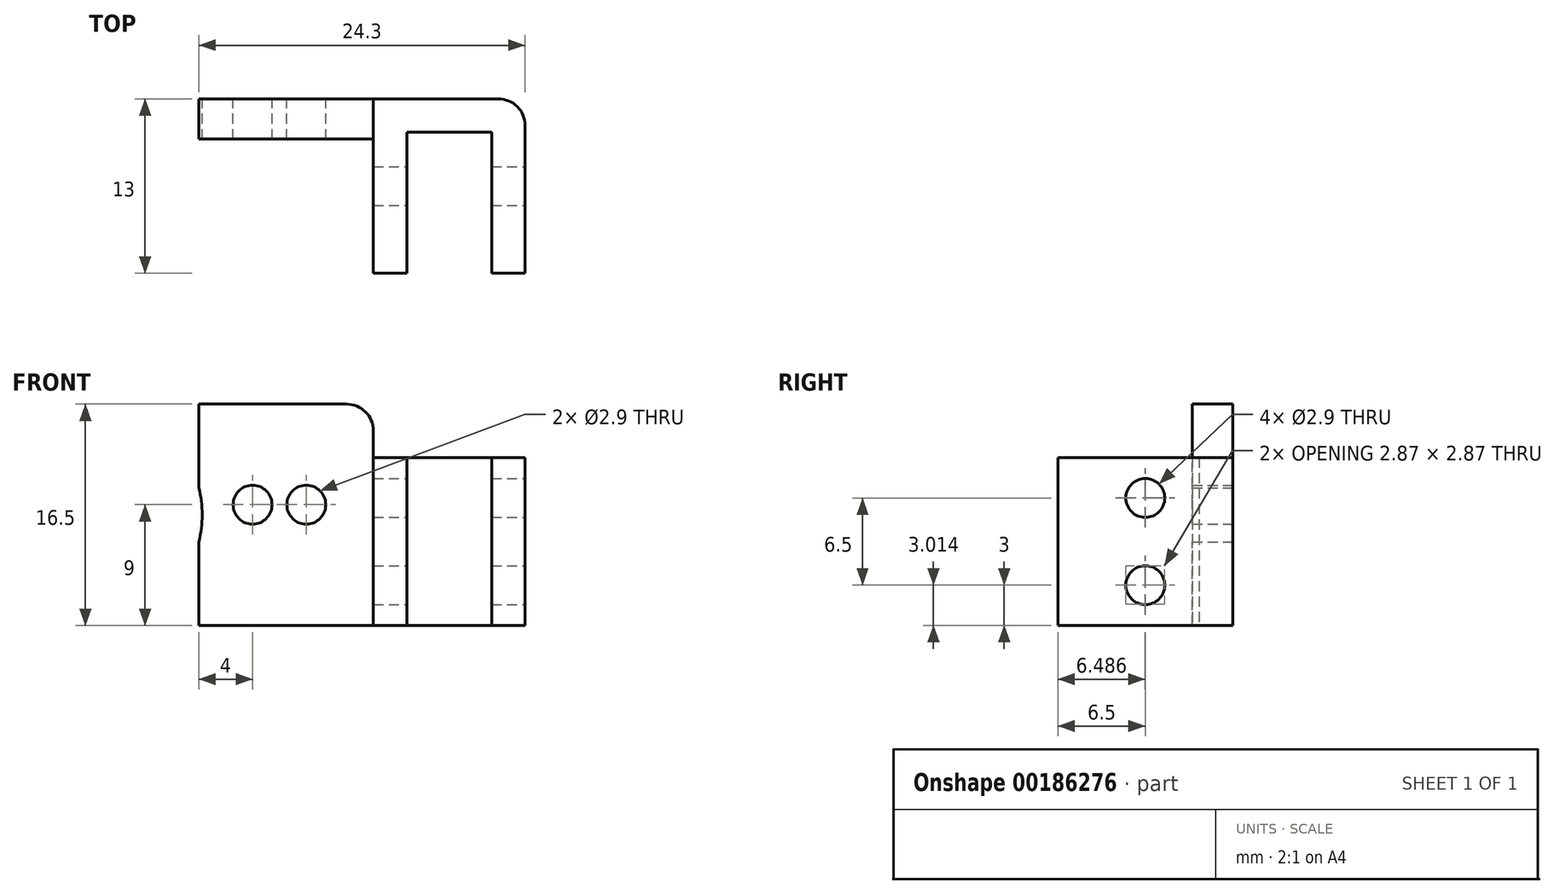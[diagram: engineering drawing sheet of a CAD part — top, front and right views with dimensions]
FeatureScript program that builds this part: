
annotation { "Feature Type Name" : "Feature", "Feature Type Description" : "" }
export const myFeature = defineFeature(function(context is Context, id is Id, definition is map)
    precondition{}
    {
        {
            var Q0;
            Q0=qCreatedBy(makeId("Top.planeOp"),FACE);
            var sketch = newSketch(context, id + "F0", { "sketchPlane" : qUnion([Q0])});
            skLineSegment(sketch, "E0.bottom", {"start": v(3.15, -4) * mm, "end": v(-3.15, -4) * mm});
            skLineSegment(sketch, "E0.top", {"start": v(3.15, 4) * mm, "end": v(-3.15, 4) * mm});
            skLineSegment(sketch, "E0.left", {"start": v(3.15, -4) * mm, "end": v(3.15, 4) * mm});
            skLineSegment(sketch, "E0.right", {"start": v(-3.15, -4) * mm, "end": v(-3.15, 4) * mm});
            skPoint(sketch, "E0.middle", {"position": v(0, 0) * mm});
            skLineSegment(sketch, "E1.0", {"start": v(5.65, 6.5) * mm, "end": v(-5.65, 6.5) * mm});
            skLineSegment(sketch, "E1.1", {"start": v(5.65, -6.5) * mm, "end": v(5.65, 6.5) * mm});
            skLineSegment(sketch, "E1.2", {"start": v(5.65, -6.5) * mm, "end": v(-5.65, -6.5) * mm});
            skLineSegment(sketch, "E1.3", {"start": v(-5.65, -6.5) * mm, "end": v(-5.65, 6.5) * mm});
            skLineSegment(sketch, "E2", {"start": v(3.15, -4) * mm, "end": v(3.15, -6.5) * mm});
            skPoint(sketch, "E2.endSnap0", {"position": v(0, -6.5) * mm});
            skLineSegment(sketch, "E3", {"start": v(3.15, -6.5) * mm, "end": v(-3.15, -6.5) * mm});
            skLineSegment(sketch, "E4", {"start": v(-3.15, -6.5) * mm, "end": v(-3.15, -4) * mm});
            skPoint(sketch, "E5", {"position": v(-5.65, 6.5) * mm});
            skPoint(sketch, "E6", {"position": v(-30.65, 6.5) * mm});
            skPoint(sketch, "E7", {"position": v(-30.65, 3.5) * mm});
            skPoint(sketch, "E8", {"position": v(-5.65, 3.5) * mm});
            skLineSegment(sketch, "E9", {"start": v(-5.65, 6.5) * mm, "end": v(-30.65, 6.5) * mm});
            skLineSegment(sketch, "E10", {"start": v(-30.65, 6.5) * mm, "end": v(-30.65, 3.5) * mm});
            skLineSegment(sketch, "E11", {"start": v(-30.65, 3.5) * mm, "end": v(-5.65, 3.5) * mm});
            skSolve(sketch);
        }
        {
            var Q0;
            {var subQ0=sQuery(id+"F0.wireOp",EDGE,"E9");Q0=makeQuery(id+"F0.imprint","IMPRINT",FACE,{"disambiguationData":[TD([[makeQuery(id+"F0.imprint","IMPRINT",EDGE,{"derivedFrom":subQ0}),1.0]])]});}
            var Q1;
            Q1=makeQuery(id+"F0.imprint","IMPRINT",FACE,{"disambiguationData":[TD([[makeQuery(id+"F0.imprint","IMPRINT",EDGE,{"derivedFrom":sQuery(id+"F0.wireOp",EDGE,"E0.top")}),-1.0]])]});
            extrude(context, id + "F1", {"entities" : qUnion([Q0, Q1]), "depth" : 12.5 * mm, "offsetDistance" : 25 * mm});
        }
        {
            var Q0;
            Q0=makeQuery(id+"F1.opExtrude","CAP_FACE",FACE,{"disambiguationData":[OSD([sQuery(id+"F0.wireOp",EDGE,"E0.top"),sQuery(id+"F0.wireOp",EDGE,"E0.left"),sQuery(id+"F0.wireOp",EDGE,"E0.right"),sQuery(id+"F0.wireOp",EDGE,"E1.0"),sQuery(id+"F0.wireOp",EDGE,"E1.1"),sQuery(id+"F0.wireOp",EDGE,"E1.2"),sQuery(id+"F0.wireOp",EDGE,"E1.3"),sQuery(id+"F0.wireOp",EDGE,"E2"),sQuery(id+"F0.wireOp",EDGE,"E4"),sQuery(id+"F0.wireOp",EDGE,"E9"),sQuery(id+"F0.wireOp",EDGE,"E10"),sQuery(id+"F0.wireOp",EDGE,"E11")])],"isStart":false});
            var sketch = newSketch(context, id + "F2", { "sketchPlane" : qUnion([Q0])});
            skPoint(sketch, "E12", {"position": v(-5.65, 3.5) * mm});
            skPoint(sketch, "E13", {"position": v(-5.65, 6.5) * mm});
            skPoint(sketch, "E14", {"position": v(-30.65, 6.5) * mm});
            skPoint(sketch, "E15", {"position": v(-30.65, 3.5) * mm});
            skLineSegment(sketch, "E16", {"start": v(-5.65, 3.5) * mm, "end": v(-5.65, 6.5) * mm});
            skSolve(sketch);
        }
        {
            var Q0;
            {var subQ0=sQuery(id+"F2.wireOp",EDGE,"E16");Q0=makeQuery(id+"F2.imprint","IMPRINT",FACE,{"disambiguationData":[TD([[makeQuery(id+"F2.imprint","IMPRINT",EDGE,{"derivedFrom":subQ0}),1.0]])]});}
            extrude(context, id + "F3", {"entities" : qUnion([Q0]), "operationType" : NewBodyOperationType.ADD, "depth" : 4 * mm, "offsetDistance" : 25 * mm});
        }
        {
            var Q0;
            Q0=makeQuery(id+"F1.opExtrude","SWEPT_FACE",FACE,{"disambiguationData":[OSD([sQuery(id+"F0.wireOp",EDGE,"E1.0"),sQuery(id+"F0.wireOp",EDGE,"E9")])]});
            var sketch = newSketch(context, id + "F4", { "sketchPlane" : qUnion([Q0])});
            skPoint(sketch, "E17", {"position": v(30.65, 8.25) * mm});
            skPoint(sketch, "E18", {"position": v(26.65, 8.25) * mm});
            skCircle(sketch, "E19", {"center": v(26.65, 8.25) * mm, "radius": 4.5 * mm});
            skCircle(sketch, "E20", {"center": v(26.65, 8.25) * mm, "radius": 8.25 * mm});
            skSolve(sketch);
        }
        {
            var Q0;
            {var subQ0=sQuery(id+"F4.wireOp",EDGE,"E20");var subQ1=sQuery(id+"F0.wireOp",EDGE,"E9");var subQ2=sQuery(id+"F0.wireOp",EDGE,"E1.0");var subQ3=makeQuery(id+"F3.opExtrude","CAP_EDGE",EDGE,{"disambiguationData":[OSD([subQ2,subQ1])],"isStart":false});var subQ4=makeQuery(id+"F4.imprint","INTERSECT",VERTEX,{"derivedFrom":[subQ3,subQ0]});Q0=makeQuery(id+"F4.imprint","IMPRINT",FACE,{"disambiguationData":[TD([[makeQuery(id+"F4.imprint","IMPRINT",EDGE,{"disambiguationData":[TD([[subQ4,1.0]])],"derivedFrom":subQ0}),-1.0]])]});}
            var Q1;
            {var subQ0=sQuery(id+"F4.wireOp",EDGE,"E20");var subQ1=sQuery(id+"F0.wireOp",EDGE,"E9");var subQ2=sQuery(id+"F0.wireOp",EDGE,"E1.0");var subQ3=makeQuery(id+"F1.opExtrude","CAP_EDGE",EDGE,{"disambiguationData":[OSD([subQ2,subQ1])],"isStart":true});var subQ4=makeQuery(id+"F4.imprint","INTERSECT",VERTEX,{"derivedFrom":[subQ3,subQ0]});Q1=makeQuery(id+"F4.imprint","IMPRINT",FACE,{"disambiguationData":[TD([[makeQuery(id+"F4.imprint","IMPRINT",EDGE,{"disambiguationData":[TD([[subQ4,-1.0]])],"derivedFrom":subQ0}),-1.0]])]});}
            var Q2;
            {var subQ0=sQuery(id+"F4.wireOp",EDGE,"E19");var subQ1=sQuery(id+"F0.wireOp",EDGE,"E10");var subQ2=sQuery(id+"F0.wireOp",EDGE,"E9");var subQ3=makeQuery(id+"F3.boolean.opBoolean","MERGE",EDGE,{"derivedFrom":[makeQuery(id+"F1.opExtrude","SWEPT_EDGE",EDGE,{"disambiguationData":[OSD([subQ2,subQ1])]}),makeQuery(id+"F3.opExtrude","SWEPT_EDGE",EDGE,{"disambiguationData":[OSD([sQuery(id+"F0.wireOp",EDGE,"E1.0"),subQ2,subQ1])]})]});var subQ4=makeQuery(id+"F4.imprint","INTERSECT",VERTEX,{"disambiguationData":[OD(0.0)],"derivedFrom":[subQ3,subQ0]});Q2=makeQuery(id+"F4.imprint","IMPRINT",FACE,{"disambiguationData":[TD([[makeQuery(id+"F4.imprint","IMPRINT",EDGE,{"disambiguationData":[TD([[subQ4,-1.0]])],"derivedFrom":subQ0}),1.0]])]});}
            extrude(context, id + "F5", {"entities" : qUnion([Q0, Q1, Q2]), "operationType" : NewBodyOperationType.REMOVE, "oppositeDirection" : true, "depth" : 25 * mm, "offsetDistance" : 25 * mm});
        }
        {
            var Q0;
            {var subQ0=sQuery(id+"F4.wireOp",EDGE,"E20");var subQ1=sQuery(id+"F0.wireOp",EDGE,"E9");var subQ2=sQuery(id+"F0.wireOp",EDGE,"E1.0");var subQ10=makeQuery(id+"F4.imprint","INTERSECT",VERTEX,{"derivedFrom":[makeQuery(id+"F3.opExtrude","CAP_EDGE",EDGE,{"disambiguationData":[OSD([subQ2,subQ1])],"isStart":false}),subQ0]});Q0=makeQuery(id+"F4.imprint","IMPRINT",FACE,{"disambiguationData":[TD([[makeQuery(id+"F4.imprint","IMPRINT",EDGE,{"disambiguationData":[TD([[subQ10,-1.0]])],"derivedFrom":subQ0}),1.0]])]});}
            extrude(context, id + "F6", {"entities" : qUnion([Q0]), "operationType" : NewBodyOperationType.ADD, "depth" : 15 * mm, "offsetDistance" : 25 * mm});
        }
        {
            var Q0;
            Q0=makeQuery(id+"F1.opExtrude","SWEPT_FACE",FACE,{"disambiguationData":[OSD([sQuery(id+"F0.wireOp",EDGE,"E1.1")])]});
            var sketch = newSketch(context, id + "F7", { "sketchPlane" : qUnion([Q0])});
            skPoint(sketch, "E21", {"position": v(4, 0) * mm});
            skPoint(sketch, "E22", {"position": v(4, 3) * mm});
            skPoint(sketch, "E23", {"position": v(0, 3) * mm});
            skPoint(sketch, "E24", {"position": v(0, 9.5) * mm});
            skSolve(sketch);
        }
        {
            var Q0;
            Q0=sQuery(id+"F7.wireOp",VERTEX,"E23");
            var Q1;
            Q1=sQuery(id+"F7.wireOp",VERTEX,"E24");
            var Q2;
            Q2=makeQuery(id+"F1.opExtrude","SWEPT_BODY",BODY,{"disambiguationData":[OSD([sQuery(id+"F0.wireOp",EDGE,"E0.top"),sQuery(id+"F0.wireOp",EDGE,"E0.left"),sQuery(id+"F0.wireOp",EDGE,"E0.right"),sQuery(id+"F0.wireOp",EDGE,"E1.0"),sQuery(id+"F0.wireOp",EDGE,"E1.1"),sQuery(id+"F0.wireOp",EDGE,"E1.2"),sQuery(id+"F0.wireOp",EDGE,"E1.3"),sQuery(id+"F0.wireOp",EDGE,"E2"),sQuery(id+"F0.wireOp",EDGE,"E4"),sQuery(id+"F0.wireOp",EDGE,"E9"),sQuery(id+"F0.wireOp",EDGE,"E10"),sQuery(id+"F0.wireOp",EDGE,"E11")])]});
            hole(context, id + "F8", {"style" : HoleStyle.SIMPLE, "endStyle" : HoleEndStyle.THROUGH, "standardTappedOrClearance" : lookupTablePath({ "fit" : "Normal", "standard" : "ISO", "size" : "M2.5", "type" : "Clearance" }), "standardBlindInLast" : lookupTablePath({ "fit" : "Normal", "standard" : "ISO", "engagement" : "75%", "pitch" : "0.35 mm", "size" : "M2.5", "type" : "Clearance & tapped" }), "holeDiameter" : 2.9 * mm, "majorDiameter" : 5 * mm, "isTappedThrough" : true, "tappedDepth" : 12 * mm, "tapClearance" : 3, "startFromSketch" : true, "locations" : qUnion([Q0, Q1]), "scope" : qUnion([Q2])});
        }
        {
            var Q0;
            Q0=makeQuery(id+"F6.opExtrude","CAP_FACE",FACE,{"disambiguationData":[OSD([sQuery(id+"F0.wireOp",EDGE,"E1.0"),sQuery(id+"F0.wireOp",EDGE,"E9"),sQuery(id+"F0.wireOp",EDGE,"E10"),sQuery(id+"F4.wireOp",EDGE,"E19"),sQuery(id+"F4.wireOp",EDGE,"E20")])],"isStart":false});
            extrude(context, id + "F9", {"entities" : qUnion([Q0]), "operationType" : NewBodyOperationType.REMOVE, "oppositeDirection" : true, "depth" : 25 * mm, "offsetDistance" : 25 * mm});
        }
        {
            var Q0;
            {var subQ1=sQuery(id+"F0.wireOp",EDGE,"E1.0");var subQ3=makeQuery(id+"F1.opExtrude","SWEPT_EDGE",EDGE,{"disambiguationData":[OSD([subQ1,sQuery(id+"F0.wireOp",EDGE,"E1.1")])]});Q0=makeQuery(id+"F4.imprint","IMPRINT",FACE,{"disambiguationData":[TD([[makeQuery(id+"F4.imprint","IMPRINT",EDGE,{"derivedFrom":subQ3}),1.0]])]});}
            var sketch = newSketch(context, id + "F10", { "sketchPlane" : qUnion([Q0])});
            skPoint(sketch, "E25", {"position": v(18.65, 9) * mm});
            skPoint(sketch, "E26", {"position": v(18.65, 16.5) * mm});
            skPoint(sketch, "E27", {"position": v(18.65, 0) * mm});
            skLineSegment(sketch, "E28", {"start": v(18.65, 0) * mm, "end": v(18.65, 16.5) * mm});
            skPoint(sketch, "E29", {"position": v(14.65, 9) * mm});
            skPoint(sketch, "E30", {"position": v(10.65, 9) * mm});
            skPoint(sketch, "E31", {"position": v(6.65, 9) * mm});
            skSolve(sketch);
        }
        {
            var Q0;
            {var subQ0=sQuery(id+"F10.wireOp",EDGE,"E28");var subQ1=sQuery(id+"F0.wireOp",EDGE,"E9");var subQ2=sQuery(id+"F0.wireOp",EDGE,"E1.0");var subQ3=makeQuery(id+"F3.opExtrude","CAP_EDGE",EDGE,{"disambiguationData":[OSD([subQ2,subQ1])],"isStart":false});var subQ4=sQuery(id+"F4.wireOp",EDGE,"E20");var subQ5=makeQuery(id+"F4.imprint","INTERSECT",VERTEX,{"derivedFrom":[subQ3,subQ4]});var subQ8=makeQuery(id+"F4.imprint","IMPRINT",EDGE,{"disambiguationData":[TD([[subQ5,-1.0]])],"derivedFrom":subQ4});var subQ9=makeQuery(id+"F10.imprint","INTERSECT",VERTEX,{"disambiguationData":[OD(1.0)],"derivedFrom":[subQ8,subQ0]});Q0=makeQuery(id+"F10.imprint","IMPRINT",FACE,{"disambiguationData":[TD([[makeQuery(id+"F10.imprint","IMPRINT",EDGE,{"disambiguationData":[TD([[subQ9,-1.0]])],"derivedFrom":subQ0}),-1.0]])]});}
            var Q1;
            {var subQ0=sQuery(id+"F10.wireOp",EDGE,"E28");var subQ1=sQuery(id+"F0.wireOp",EDGE,"E9");var subQ2=sQuery(id+"F0.wireOp",EDGE,"E1.0");var subQ4=sQuery(id+"F4.wireOp",EDGE,"E20");var subQ8=makeQuery(id+"F4.imprint","IMPRINT",EDGE,{"disambiguationData":[TD([[makeQuery(id+"F4.imprint","INTERSECT",VERTEX,{"derivedFrom":[makeQuery(id+"F3.opExtrude","CAP_EDGE",EDGE,{"disambiguationData":[OSD([subQ2,subQ1])],"isStart":false}),subQ4]}),-1.0]])],"derivedFrom":subQ4});var subQ9=makeQuery(id+"F10.imprint","INTERSECT",VERTEX,{"disambiguationData":[OD(0.0)],"derivedFrom":[subQ8,subQ0]});Q1=makeQuery(id+"F10.imprint","IMPRINT",FACE,{"disambiguationData":[TD([[makeQuery(id+"F10.imprint","IMPRINT",EDGE,{"disambiguationData":[TD([[subQ9,1.0]])],"derivedFrom":subQ0}),-1.0]])]});}
            extrude(context, id + "F11", {"entities" : qUnion([Q0, Q1]), "operationType" : NewBodyOperationType.REMOVE, "oppositeDirection" : true, "depth" : 25 * mm, "offsetDistance" : 25 * mm});
        }
        {
            var Q0;
            {var subQ0=sQuery(id+"F10.wireOp",EDGE,"E28");var subQ1=sQuery(id+"F0.wireOp",EDGE,"E9");var subQ2=sQuery(id+"F0.wireOp",EDGE,"E1.0");var subQ3=makeQuery(id+"F1.opExtrude","CAP_EDGE",EDGE,{"disambiguationData":[OSD([subQ2,subQ1])],"isStart":true});Q0=makeQuery(id+"F11.boolean.opBoolean","COPY",EDGE,{"derivedFrom":makeQuery(id+"F11.opExtrude","SWEPT_EDGE",EDGE,{"disambiguationData":[OSD([subQ2,subQ1,subQ0]),TDD([makeQuery(id+"F10.imprint","INTERSECT",VERTEX,{"derivedFrom":[makeQuery(id+"F4.imprint","IMPRINT",EDGE,{"disambiguationData":[TD([[makeQuery(id+"F4.imprint","INTERSECT",VERTEX,{"derivedFrom":[subQ3,sQuery(id+"F4.wireOp",EDGE,"E20")]}),1.0]])],"derivedFrom":subQ3}),subQ0]})])]})});}
            var Q1;
            {var subQ0=sQuery(id+"F10.wireOp",EDGE,"E28");var subQ1=sQuery(id+"F0.wireOp",EDGE,"E9");var subQ2=sQuery(id+"F0.wireOp",EDGE,"E1.0");var subQ3=makeQuery(id+"F3.opExtrude","CAP_EDGE",EDGE,{"disambiguationData":[OSD([subQ2,subQ1])],"isStart":false});Q1=makeQuery(id+"F11.boolean.opBoolean","COPY",EDGE,{"derivedFrom":makeQuery(id+"F11.opExtrude","SWEPT_EDGE",EDGE,{"disambiguationData":[OSD([subQ2,subQ1,subQ0]),TDD([makeQuery(id+"F10.imprint","INTERSECT",VERTEX,{"derivedFrom":[makeQuery(id+"F4.imprint","IMPRINT",EDGE,{"disambiguationData":[TD([[makeQuery(id+"F4.imprint","INTERSECT",VERTEX,{"derivedFrom":[subQ3,sQuery(id+"F4.wireOp",EDGE,"E20")]}),1.0]])],"derivedFrom":subQ3}),subQ0]})])]})});}
            var Q2;
            Q2=makeQuery(id+"F3.opExtrude","CAP_EDGE",EDGE,{"disambiguationData":[OSD([sQuery(id+"F2.wireOp",EDGE,"E16")])],"isStart":false});
            var Q3;
            Q3=makeQuery(id+"F1.opExtrude","SWEPT_EDGE",EDGE,{"disambiguationData":[OSD([sQuery(id+"F0.wireOp",EDGE,"E1.0"),sQuery(id+"F0.wireOp",EDGE,"E1.1")])]});
            fillet(context, id + "F12", {"entities" : qUnion([Q0, Q1, Q2, Q3]), "tangentPropagation" : true, "radius" : 2 * mm, "defaultsChanged" : false, "vertexSettings" : [], "allowEdgeOverflow" : false});
        }
        {
            var Q0;
            Q0=sQuery(id+"F10.wireOp",VERTEX,"E29");
            var Q1;
            Q1=sQuery(id+"F10.wireOp",VERTEX,"E30");
            var Q2;
            Q2=makeQuery(id+"F1.opExtrude","SWEPT_BODY",BODY,{"disambiguationData":[OSD([sQuery(id+"F0.wireOp",EDGE,"E0.top"),sQuery(id+"F0.wireOp",EDGE,"E0.left"),sQuery(id+"F0.wireOp",EDGE,"E0.right"),sQuery(id+"F0.wireOp",EDGE,"E1.0"),sQuery(id+"F0.wireOp",EDGE,"E1.1"),sQuery(id+"F0.wireOp",EDGE,"E1.2"),sQuery(id+"F0.wireOp",EDGE,"E1.3"),sQuery(id+"F0.wireOp",EDGE,"E2"),sQuery(id+"F0.wireOp",EDGE,"E4"),sQuery(id+"F0.wireOp",EDGE,"E9"),sQuery(id+"F0.wireOp",EDGE,"E10"),sQuery(id+"F0.wireOp",EDGE,"E11")])]});
            hole(context, id + "F13", {"style" : HoleStyle.SIMPLE, "endStyle" : HoleEndStyle.THROUGH, "standardTappedOrClearance" : lookupTablePath({ "fit" : "Normal", "standard" : "ISO", "size" : "M2.5", "type" : "Clearance" }), "standardBlindInLast" : lookupTablePath({ "fit" : "Normal", "standard" : "ISO", "engagement" : "75%", "pitch" : "0.35 mm", "size" : "M2.5", "type" : "Clearance & tapped" }), "holeDiameter" : 2.9 * mm, "majorDiameter" : 5 * mm, "isTappedThrough" : true, "tappedDepth" : 12 * mm, "tapClearance" : 3, "startFromSketch" : true, "locations" : qUnion([Q0, Q1]), "scope" : qUnion([Q2])});
        }
    });
